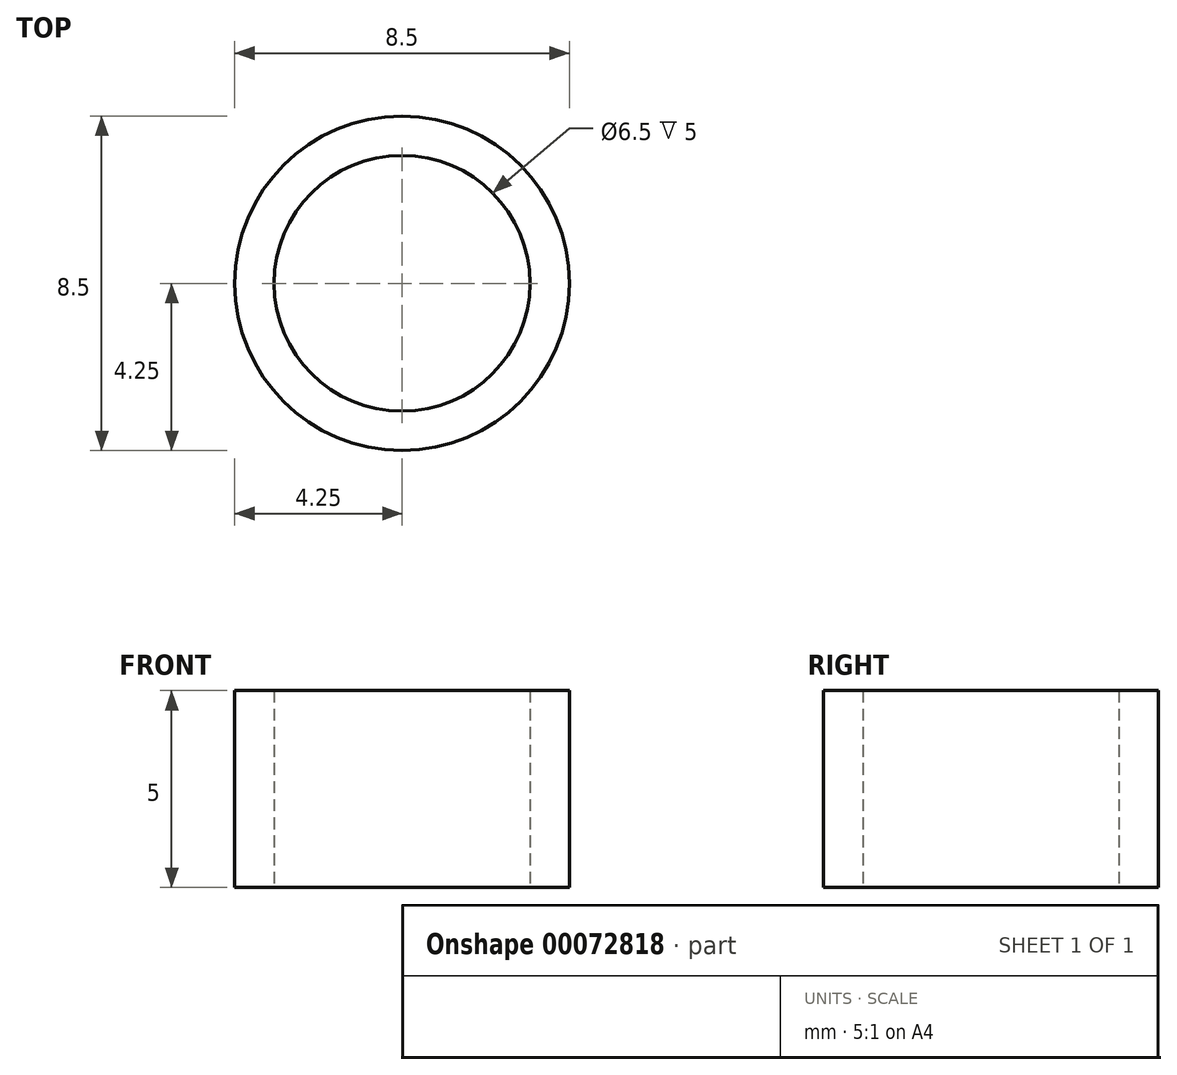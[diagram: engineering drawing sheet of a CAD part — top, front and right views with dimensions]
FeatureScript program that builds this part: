
annotation { "Feature Type Name" : "Feature", "Feature Type Description" : "" }
export const myFeature = defineFeature(function(context is Context, id is Id, definition is map)
    precondition{}
    {
        {
            var Q0;
            Q0=qCreatedBy(makeId("Top.planeOp"),FACE);
            var sketch = newSketch(context, id + "F0", { "sketchPlane" : qUnion([Q0])});
            skCircle(sketch, "E0", {"center": v(0, 0) * mm, "radius": 3.25 * mm});
            skCircle(sketch, "E1", {"center": v(0, 0) * mm, "radius": 4.25 * mm});
            skSolve(sketch);
        }
        {
            var Q0;
            Q0 = qSketchRegion(id + "F0", true);
            var Q1;
            Q1=makeQuery(id+"F0.imprint","IMPRINT",FACE,{"disambiguationData":[TD([[makeQuery(id+"F0.imprint","IMPRINT",EDGE,{"derivedFrom":sQuery(id+"F0.wireOp",EDGE,"E0")}),-1.0]])]});
            extrude(context, id + "F1", {"entities" : qUnion([Q0, Q1]), "depth" : 5 * mm});
        }
    });
